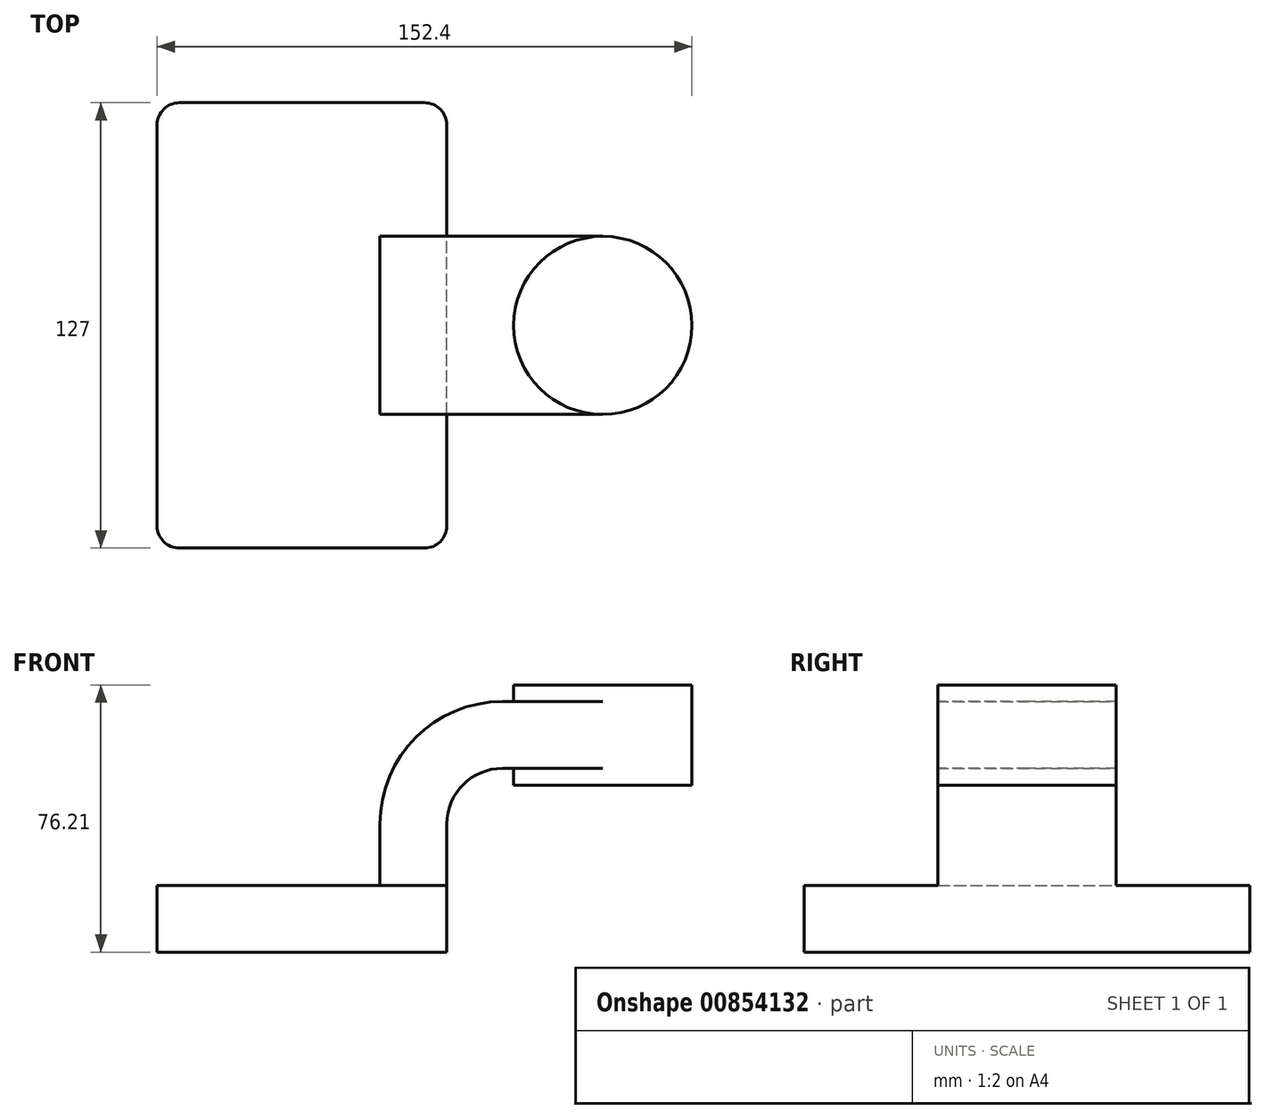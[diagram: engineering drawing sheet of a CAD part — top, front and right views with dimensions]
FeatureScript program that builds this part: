
annotation { "Feature Type Name" : "Feature", "Feature Type Description" : "" }
export const myFeature = defineFeature(function(context is Context, id is Id, definition is map)
    precondition{}
    {
        {
            var Q0;
            Q0=qCreatedBy(makeId("Front.planeOp"),FACE);
            var sketch = newSketch(context, id + "F0", { "sketchPlane" : qUnion([Q0])});
            skLineSegment(sketch, "E0.bottom", {"start": v(41.27, 9.53) * mm, "end": v(-41.28, 9.53) * mm});
            skLineSegment(sketch, "E0.top", {"start": v(41.28, -9.52) * mm, "end": v(-41.27, -9.52) * mm});
            skLineSegment(sketch, "E0.left", {"start": v(41.28, 9.53) * mm, "end": v(41.28, -9.52) * mm});
            skLineSegment(sketch, "E0.right", {"start": v(-41.28, 9.53) * mm, "end": v(-41.27, -9.52) * mm});
            skPoint(sketch, "E0.middle", {"position": v(0, 0) * mm});
            skLineSegment(sketch, "E1.bottom", {"start": v(111.12, 66.68) * mm, "end": v(60.32, 66.68) * mm});
            skLineSegment(sketch, "E1.top", {"start": v(111.12, 38.1) * mm, "end": v(60.33, 38.1) * mm});
            skLineSegment(sketch, "E1.left", {"start": v(111.12, 66.68) * mm, "end": v(111.12, 38.1) * mm});
            skLineSegment(sketch, "E1.right", {"start": v(60.32, 66.68) * mm, "end": v(60.33, 38.1) * mm});
            skPoint(sketch, "E1.middle", {"position": v(85.72, 52.39) * mm});
            skLineSegment(sketch, "E2", {"start": v(41.27, 9.53) * mm, "end": v(41.27, 27) * mm});
            skArc(sketch, "E3", {"start": v(41.27, 27) * mm, "mid": v(45.92, 38.23) * mm, "end": v(57.15, 42.88) * mm});
            skLineSegment(sketch, "E4", {"start": v(57.15, 42.88) * mm, "end": v(85.72, 42.88) * mm});
            skLineSegment(sketch, "E5.0", {"start": v(57.15, 61.93) * mm, "end": v(94.03, 61.93) * mm});
            skArc(sketch, "E5.1", {"start": v(22.23, 27) * mm, "mid": v(32.45, 51.7) * mm, "end": v(57.15, 61.93) * mm});
            skLineSegment(sketch, "E5.2", {"start": v(22.22, 9.53) * mm, "end": v(22.22, 27) * mm});
            skLineSegment(sketch, "E6", {"start": v(85.72, 38.1) * mm, "end": v(85.72, 66.68) * mm});
            skFitSpline(sketch, "E7", {"points": [v(-41.28, 9.53) * mm, v(57.15, 61.93) * mm], "startDerivative": vector(85.89, 94.4) * mm, "endDerivative": vector(99.74, -2.4) * mm});
            skSolve(sketch);
        }
        {
            var Q0;
            Q0=makeQuery(id+"F0.imprint","IMPRINT",FACE,{"disambiguationData":[TD([[makeQuery(id+"F0.imprint","IMPRINT",EDGE,{"derivedFrom":sQuery(id+"F0.wireOp",EDGE,"E0.top")}),-1.0]])]});
            extrude(context, id + "F1", {"entities" : qUnion([Q0]), "endBound" : BoundingType.SYMMETRIC, "depth" : 127 * mm, "offsetDistance" : 25.4 * mm});
        }
        {
            var Q0;
            {var subQ1=sQuery(id+"F0.wireOp",EDGE,"E2");Q0=makeQuery(id+"F0.imprint","IMPRINT",FACE,{"disambiguationData":[TD([[makeQuery(id+"F0.imprint","IMPRINT",EDGE,{"derivedFrom":subQ1}),1.0]])]});}
            var Q1;
            {var subQ0=sQuery(id+"F0.wireOp",EDGE,"E5.0");var subQ1=sQuery(id+"F0.wireOp",EDGE,"E1.right");var subQ2=makeQuery(id+"F0.imprint","INTERSECT",VERTEX,{"derivedFrom":[subQ1,subQ0]});Q1=makeQuery(id+"F0.imprint","IMPRINT",FACE,{"disambiguationData":[TD([[makeQuery(id+"F0.imprint","IMPRINT",EDGE,{"disambiguationData":[TD([[subQ2,-1.0]])],"derivedFrom":subQ1}),1.0]])]});}
            extrude(context, id + "F2", {"entities" : qUnion([Q0, Q1]), "operationType" : NewBodyOperationType.ADD, "endBound" : BoundingType.SYMMETRIC, "depth" : 50.8 * mm, "offsetDistance" : 25.4 * mm});
        }
        {
            var Q0;
            Q0=makeQuery(id+"F0.imprint","IMPRINT",FACE,{"disambiguationData":[TD([[makeQuery(id+"F0.imprint","IMPRINT",EDGE,{"derivedFrom":sQuery(id+"F0.wireOp",EDGE,"E5.1")}),1.0]])]});
            extrude(context, id + "F3", {"entities" : qUnion([Q0]), "operationType" : NewBodyOperationType.ADD, "endBound" : BoundingType.SYMMETRIC, "depth" : 15.88 * mm, "offsetDistance" : 25.4 * mm});
        }
        {
            var Q0;
            {var subQ4=sQuery(id+"F0.wireOp",EDGE,"E1.left");Q0=makeQuery(id+"F0.imprint","IMPRINT",FACE,{"disambiguationData":[TD([[makeQuery(id+"F0.imprint","IMPRINT",EDGE,{"derivedFrom":subQ4}),-1.0]])]});}
            var Q1;
            Q1=sQuery(id+"F0.wireOp",EDGE,"E6");
            revolve(context, id + "F4", {"operationType" : NewBodyOperationType.ADD, "surfaceOperationType" : NewSurfaceOperationType.NEW, "entities" : qUnion([Q0]), "axis" : qUnion([Q1]), "revolveType" : RevolveType.FULL});
        }
        {
            var Q0;
            Q0=makeQuery(id+"F1.opExtrude","CAP_EDGE",EDGE,{"disambiguationData":[OSD([sQuery(id+"F0.wireOp",EDGE,"E0.right")])],"isStart":false});
            var Q1;
            Q1=makeQuery(id+"F1.opExtrude","CAP_EDGE",EDGE,{"disambiguationData":[OSD([sQuery(id+"F0.wireOp",EDGE,"E0.left")])],"isStart":false});
            var Q2;
            Q2=makeQuery(id+"F1.opExtrude","CAP_EDGE",EDGE,{"disambiguationData":[OSD([sQuery(id+"F0.wireOp",EDGE,"E0.left")])],"isStart":true});
            var Q3;
            Q3=makeQuery(id+"F1.opExtrude","CAP_EDGE",EDGE,{"disambiguationData":[OSD([sQuery(id+"F0.wireOp",EDGE,"E0.right")])],"isStart":true});
            fillet(context, id + "F5", {"entities" : qUnion([Q0, Q1, Q2, Q3]), "radius" : 6.35 * mm, "tangentPropagation" : true, "allowEdgeOverflow" : false});
        }
    });
